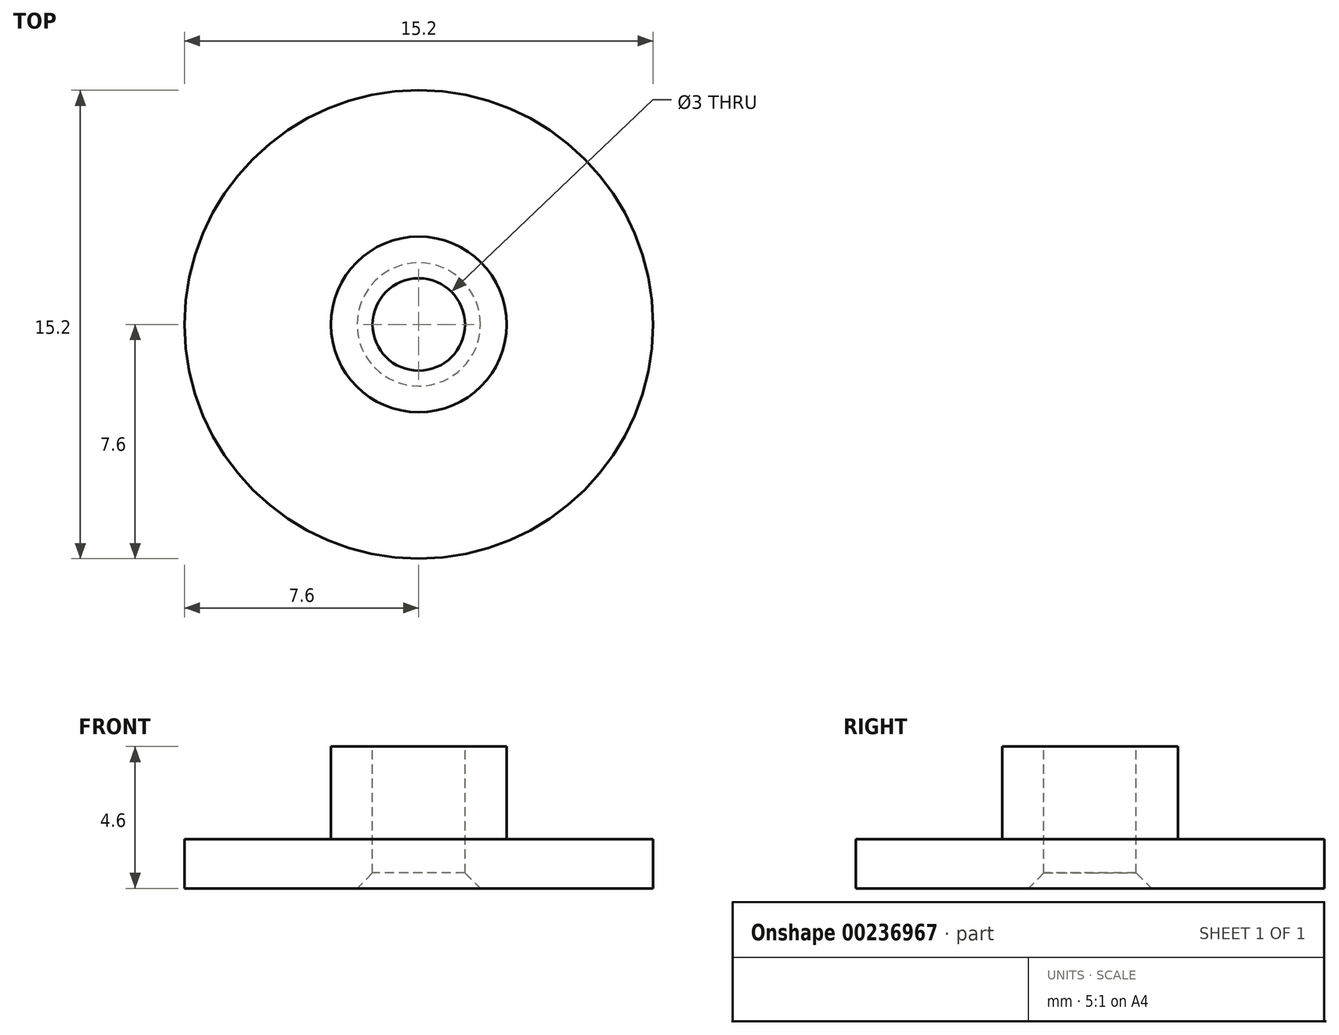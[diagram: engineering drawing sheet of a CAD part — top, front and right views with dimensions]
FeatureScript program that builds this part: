
annotation { "Feature Type Name" : "Feature", "Feature Type Description" : "" }
export const myFeature = defineFeature(function(context is Context, id is Id, definition is map)
    precondition{}
    {
        {
            var Q0;
            Q0=qCreatedBy(makeId("Top.planeOp"),FACE);
            var sketch = newSketch(context, id + "F0", { "sketchPlane" : qUnion([Q0])});
            skCircle(sketch, "E0", {"center": v(0, 0) * mm, "radius": 7.6 * mm});
            skSolve(sketch);
        }
        {
            var Q0;
            Q0 = qSketchRegion(id + "F0", true);
            extrude(context, id + "F1", {"entities" : qUnion([Q0]), "depth" : 1.6 * mm});
        }
        {
            var Q0;
            Q0=makeQuery(id+"F1.opExtrude","CAP_FACE",FACE,{"disambiguationData":[OSD([sQuery(id+"F0.wireOp",EDGE,"E0")])],"isStart":false});
            var sketch = newSketch(context, id + "F2", { "sketchPlane" : qUnion([Q0])});
            skCircle(sketch, "E1", {"center": v(0, 0) * mm, "radius": 2.85 * mm});
            skSolve(sketch);
        }
        {
            var Q0;
            Q0 = qSketchRegion(id + "F2", true);
            extrude(context, id + "F3", {"entities" : qUnion([Q0]), "operationType" : NewBodyOperationType.ADD, "depth" : 3 * mm});
        }
        {
            var Q0;
            Q0=makeQuery(id+"F3.opExtrude","CAP_FACE",FACE,{"disambiguationData":[OSD([sQuery(id+"F2.wireOp",EDGE,"E1")])],"isStart":false});
            var sketch = newSketch(context, id + "F4", { "sketchPlane" : qUnion([Q0])});
            skCircle(sketch, "E2", {"center": v(0, 0) * mm, "radius": 1.5 * mm});
            skSolve(sketch);
        }
        {
            var Q0;
            Q0 = qSketchRegion(id + "F4", true);
            extrude(context, id + "F5", {"entities" : qUnion([Q0]), "operationType" : NewBodyOperationType.REMOVE, "oppositeDirection" : true, "depth" : 25 * mm});
        }
        {
            var Q0;
            Q0=makeQuery(id+"F5.boolean.opBoolean","INTERSECT",EDGE,{"derivedFrom":[makeQuery(id+"F1.opExtrude","CAP_FACE",FACE,{"disambiguationData":[OSD([sQuery(id+"F0.wireOp",EDGE,"E0")])],"isStart":true}),makeQuery(id+"F5.opExtrude","SWEPT_FACE",FACE,{"disambiguationData":[OSD([sQuery(id+"F4.wireOp",EDGE,"E2")])]})]});
            chamfer(context, id + "F6", {"entities" : qUnion([Q0]), "width" : 0.5 * mm, "tangentPropagation" : true});
        }
    });
